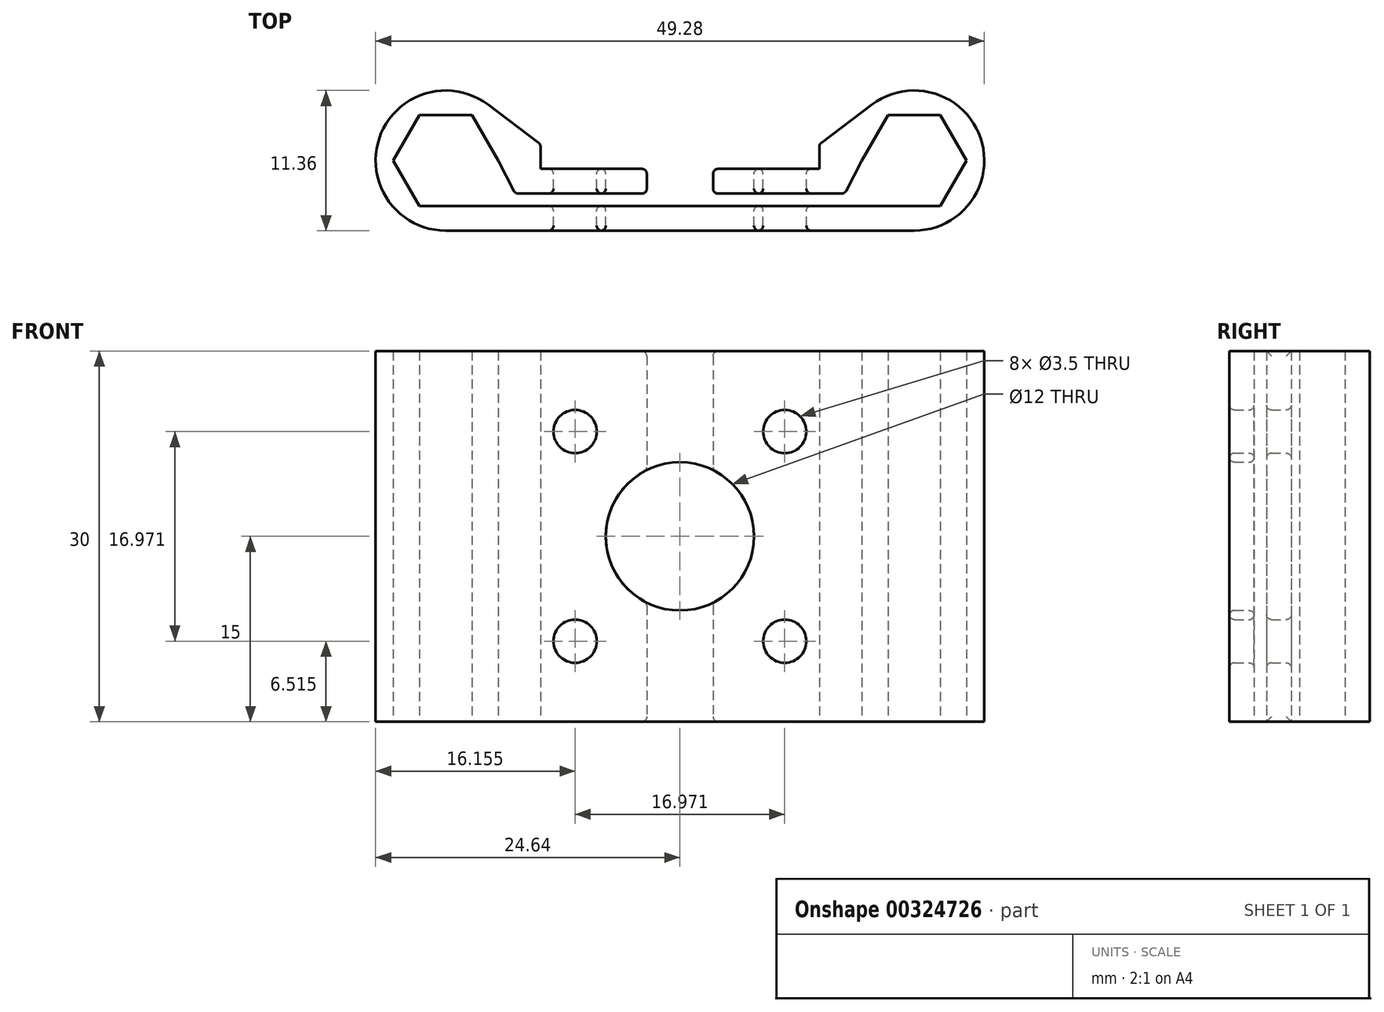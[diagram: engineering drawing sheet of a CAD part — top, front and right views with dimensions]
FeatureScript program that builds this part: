
annotation { "Feature Type Name" : "Feature", "Feature Type Description" : "" }
export const myFeature = defineFeature(function(context is Context, id is Id, definition is map)
    precondition{}
    {
        {
            var Q0;
            Q0=qCreatedBy(makeId("Front.planeOp"),FACE);
            var sketch = newSketch(context, id + "F0", { "sketchPlane" : qUnion([Q0])});
            skCircle(sketch, "E0", {"center": v(0, 0) * mm, "radius": 17.5 * mm});
            skCircle(sketch, "E1", {"center": v(0, 0) * mm, "radius": 6 * mm});
            skLineSegment(sketch, "E2", {"start": v(12.37, 12.37) * mm, "end": v(-12.37, -12.37) * mm, "construction": true});
            skLineSegment(sketch, "E3", {"start": v(0, 0) * mm, "end": v(-17.5, 0) * mm, "construction": true});
            skLineSegment(sketch, "E4", {"start": v(12.37, -12.37) * mm, "end": v(-12.37, 12.37) * mm, "construction": true});
            skCircle(sketch, "E5.0", {"center": v(0, 0) * mm, "radius": 12 * mm, "construction": true});
            skPoint(sketch, "E6", {"position": v(-8.49, -8.49) * mm});
            skPoint(sketch, "E7", {"position": v(8.49, -8.49) * mm});
            skPoint(sketch, "E8", {"position": v(8.49, 8.49) * mm});
            skPoint(sketch, "E9", {"position": v(-8.49, 8.49) * mm});
            skCircle(sketch, "E10", {"center": v(-8.49, -8.49) * mm, "radius": 1.75 * mm});
            skCircle(sketch, "E11", {"center": v(8.49, -8.49) * mm, "radius": 1.75 * mm});
            skCircle(sketch, "E12", {"center": v(8.49, 8.49) * mm, "radius": 1.75 * mm});
            skCircle(sketch, "E13", {"center": v(-8.49, 8.49) * mm, "radius": 1.75 * mm});
            skSolve(sketch);
        }
        {
            var Q0;
            Q0=qCreatedBy(makeId("Top.planeOp"),FACE);
            var sketch = newSketch(context, id + "F1", { "sketchPlane" : qUnion([Q0])});
            skPoint(sketch, "E14.0", {"position": v(-8.49, 0) * mm});
            skPoint(sketch, "E15.0", {"position": v(8.49, 0) * mm});
            skLineSegment(sketch, "E16", {"start": v(0, 0) * mm, "end": v(-18.96, 0) * mm, "construction": true});
            skCircle(sketch, "E17.cCircle", {"center": v(-18.96, 0) * mm, "radius": 3.67 * mm, "construction": true});
            skLineSegment(sketch, "E17.0", {"start": v(-16.84, -3.68) * mm, "end": v(-21.08, -3.68) * mm});
            skLineSegment(sketch, "E17.1", {"start": v(-21.08, -3.67) * mm, "end": v(-23.2, 0) * mm});
            skLineSegment(sketch, "E17.2", {"start": v(-23.2, 0) * mm, "end": v(-21.08, 3.68) * mm});
            skLineSegment(sketch, "E17.3", {"start": v(-21.08, 3.67) * mm, "end": v(-16.84, 3.67) * mm});
            skLineSegment(sketch, "E17.4", {"start": v(-16.84, 3.67) * mm, "end": v(-14.72, 0) * mm});
            skLineSegment(sketch, "E17.5", {"start": v(-14.72, 0) * mm, "end": v(-16.84, -3.68) * mm});
            skPoint(sketch, "E17.0.midPoint", {"position": v(-18.96, -3.68) * mm});
            skLineSegment(sketch, "E18", {"start": v(0, 0) * mm, "end": v(18.96, 0) * mm, "construction": true});
            skCircle(sketch, "E19.cCircle", {"center": v(18.96, 0) * mm, "radius": 3.67 * mm, "construction": true});
            skLineSegment(sketch, "E19.0", {"start": v(21.08, -3.67) * mm, "end": v(16.84, -3.68) * mm});
            skLineSegment(sketch, "E19.1", {"start": v(16.84, -3.67) * mm, "end": v(14.72, 0) * mm});
            skLineSegment(sketch, "E19.2", {"start": v(14.72, 0) * mm, "end": v(16.84, 3.67) * mm});
            skLineSegment(sketch, "E19.3", {"start": v(16.84, 3.67) * mm, "end": v(21.08, 3.68) * mm});
            skLineSegment(sketch, "E19.4", {"start": v(21.08, 3.67) * mm, "end": v(23.2, 0) * mm});
            skLineSegment(sketch, "E19.5", {"start": v(23.2, 0) * mm, "end": v(21.08, -3.67) * mm});
            skPoint(sketch, "E19.0.midPoint", {"position": v(18.96, -3.67) * mm});
            skLineSegment(sketch, "E20", {"start": v(16.84, -3.67) * mm, "end": v(-16.84, -3.68) * mm});
            skCircle(sketch, "E21.0", {"center": v(-18.96, 0) * mm, "radius": 5.67 * mm});
            skCircle(sketch, "E22.0", {"center": v(18.96, 0) * mm, "radius": 5.67 * mm});
            skLineSegment(sketch, "E23", {"start": v(-18.96, -5.68) * mm, "end": v(18.96, -5.67) * mm});
            skPoint(sketch, "E24", {"position": v(-11.29, 0) * mm});
            skPoint(sketch, "E25", {"position": v(-5.69, 0) * mm});
            skLineSegment(sketch, "E26.0", {"start": v(15.55, -2.67) * mm, "end": v(-15.55, -2.68) * mm, "construction": true});
            skLineSegment(sketch, "E27", {"start": v(-14.62, -2.68) * mm, "end": v(-2.69, -2.67) * mm});
            skLineSegment(sketch, "E28", {"start": v(-2.69, -2.67) * mm, "end": v(-2.69, -0.67) * mm});
            skLineSegment(sketch, "E29", {"start": v(-2.69, -0.67) * mm, "end": v(-13.33, -0.67) * mm});
            skLineSegment(sketch, "E30", {"start": v(-11.29, -2.68) * mm, "end": v(-11.29, -0.68) * mm, "construction": true});
            skLineSegment(sketch, "E31", {"start": v(-5.69, -2.67) * mm, "end": v(-5.69, -0.67) * mm, "construction": true});
            skLineSegment(sketch, "E32", {"start": v(-15.55, 4.53) * mm, "end": v(-11.29, 1.32) * mm});
            skLineSegment(sketch, "E33", {"start": v(-11.29, 1.32) * mm, "end": v(-11.29, -0.68) * mm});
            skLineSegment(sketch, "E34", {"start": v(-14.72, 0) * mm, "end": v(-13.33, -2.68) * mm});
            skLineSegment(sketch, "E35", {"start": v(0, 0) * mm, "end": v(0, -5.68) * mm, "construction": true});
            skLineSegment(sketch, "E36.MirrorCS", {"start": v(15.55, 4.53) * mm, "end": v(11.29, 1.32) * mm});
            skLineSegment(sketch, "E37.MirrorCS", {"start": v(11.29, 1.32) * mm, "end": v(11.29, -0.68) * mm});
            skLineSegment(sketch, "E38.MirrorCS", {"start": v(2.69, -0.67) * mm, "end": v(13.33, -0.67) * mm});
            skLineSegment(sketch, "E39.MirrorCS", {"start": v(2.69, -2.67) * mm, "end": v(2.69, -0.67) * mm});
            skLineSegment(sketch, "E40.MirrorCS", {"start": v(-15.55, -2.67) * mm, "end": v(15.55, -2.68) * mm, "construction": true});
            skLineSegment(sketch, "E41.MirrorCS", {"start": v(14.72, 0) * mm, "end": v(13.33, -2.68) * mm});
            skLineSegment(sketch, "E42", {"start": v(2.69, -2.67) * mm, "end": v(13.33, -2.67) * mm});
            skSolve(sketch);
        }
        {
            var Q0;
            {var subQ5=sQuery(id+"F1.wireOp",EDGE,"E23");Q0=makeQuery(id+"F1.imprint","IMPRINT",FACE,{"disambiguationData":[TD([[makeQuery(id+"F1.imprint","IMPRINT",EDGE,{"derivedFrom":subQ5}),1.0]])]});}
            var Q1;
            {var subQ9=sQuery(id+"F1.wireOp",EDGE,"E17.0");Q1=makeQuery(id+"F1.imprint","IMPRINT",FACE,{"disambiguationData":[TD([[makeQuery(id+"F1.imprint","IMPRINT",EDGE,{"derivedFrom":subQ9}),1.0]])]});}
            var Q2;
            {var subQ1=sQuery(id+"F1.wireOp",EDGE,"E28");Q2=makeQuery(id+"F1.imprint","IMPRINT",FACE,{"disambiguationData":[TD([[makeQuery(id+"F1.imprint","IMPRINT",EDGE,{"derivedFrom":subQ1}),1.0]])]});}
            var Q3;
            {var subQ3=sQuery(id+"F1.wireOp",EDGE,"E32");Q3=makeQuery(id+"F1.imprint","IMPRINT",FACE,{"disambiguationData":[TD([[makeQuery(id+"F1.imprint","IMPRINT",EDGE,{"derivedFrom":subQ3}),-1.0]])]});}
            var Q4;
            {var subQ6=sQuery(id+"F1.wireOp",EDGE,"E19.0");Q4=makeQuery(id+"F1.imprint","IMPRINT",FACE,{"disambiguationData":[TD([[makeQuery(id+"F1.imprint","IMPRINT",EDGE,{"derivedFrom":subQ6}),1.0]])]});}
            var Q5;
            {var subQ0=sQuery(id+"F1.wireOp",EDGE,"E36.MirrorCS");Q5=makeQuery(id+"F1.imprint","IMPRINT",FACE,{"disambiguationData":[TD([[makeQuery(id+"F1.imprint","IMPRINT",EDGE,{"derivedFrom":subQ0}),1.0]])]});}
            var Q6;
            {var subQ0=sQuery(id+"F1.wireOp",EDGE,"E39.MirrorCS");Q6=makeQuery(id+"F1.imprint","IMPRINT",FACE,{"disambiguationData":[TD([[makeQuery(id+"F1.imprint","IMPRINT",EDGE,{"derivedFrom":subQ0}),-1.0]])]});}
            extrude(context, id + "F2", {"entities" : qUnion([Q0, Q1, Q2, Q3, Q4, Q5, Q6]), "endBound" : BoundingType.SYMMETRIC, "depth" : 30 * mm});
        }
        {
            var Q0;
            Q0=makeQuery(id+"F0.imprint","IMPRINT",FACE,{"disambiguationData":[TD([[makeQuery(id+"F0.imprint","IMPRINT",EDGE,{"derivedFrom":sQuery(id+"F0.wireOp",EDGE,"E10")}),1.0]])]});
            var Q1;
            Q1=makeQuery(id+"F0.imprint","IMPRINT",FACE,{"disambiguationData":[TD([[makeQuery(id+"F0.imprint","IMPRINT",EDGE,{"derivedFrom":sQuery(id+"F0.wireOp",EDGE,"E13")}),1.0]])]});
            var Q2;
            Q2=makeQuery(id+"F0.imprint","IMPRINT",FACE,{"disambiguationData":[TD([[makeQuery(id+"F0.imprint","IMPRINT",EDGE,{"derivedFrom":sQuery(id+"F0.wireOp",EDGE,"E11")}),1.0]])]});
            var Q3;
            Q3=makeQuery(id+"F0.imprint","IMPRINT",FACE,{"disambiguationData":[TD([[makeQuery(id+"F0.imprint","IMPRINT",EDGE,{"derivedFrom":sQuery(id+"F0.wireOp",EDGE,"E12")}),1.0]])]});
            var Q4;
            Q4=makeQuery(id+"F0.imprint","IMPRINT",FACE,{"disambiguationData":[TD([[makeQuery(id+"F0.imprint","IMPRINT",EDGE,{"derivedFrom":sQuery(id+"F0.wireOp",EDGE,"E1")}),1.0]])]});
            extrude(context, id + "F3", {"entities" : qUnion([Q0, Q1, Q2, Q3, Q4]), "operationType" : NewBodyOperationType.REMOVE, "endBound" : BoundingType.THROUGH_ALL, "depth" : 25 * mm});
        }
        {
            var Q0;
            Q0=makeQuery(id+"F2.opExtrude","SWEPT_EDGE",EDGE,{"disambiguationData":[OSD([sQuery(id+"F1.wireOp",EDGE,"E27"),sQuery(id+"F1.wireOp",EDGE,"E34")])]});
            var Q1;
            Q1=makeQuery(id+"F2.opExtrude","SWEPT_EDGE",EDGE,{"disambiguationData":[OSD([sQuery(id+"F1.wireOp",EDGE,"E41.MirrorCS"),sQuery(id+"F1.wireOp",EDGE,"E42")])]});
            var Q2;
            Q2=makeQuery(id+"F2.opExtrude","SWEPT_EDGE",EDGE,{"disambiguationData":[OSD([sQuery(id+"F1.wireOp",EDGE,"E36.MirrorCS"),sQuery(id+"F1.wireOp",EDGE,"E37.MirrorCS")])]});
            var Q3;
            Q3=makeQuery(id+"F2.opExtrude","SWEPT_EDGE",EDGE,{"disambiguationData":[OSD([sQuery(id+"F1.wireOp",EDGE,"E32"),sQuery(id+"F1.wireOp",EDGE,"E33")])]});
            var Q4;
            Q4=makeQuery(id+"F3.boolean.opBoolean","COPY",FACE,{"disambiguationData":[TD([makeQuery(id+"F2.opExtrude","SWEPT_FACE",FACE,{"disambiguationData":[OSD([sQuery(id+"F1.wireOp",EDGE,"E27")])]})])],"derivedFrom":makeQuery(id+"F3.opExtrude","SWEPT_FACE",FACE,{"disambiguationData":[OSD([sQuery(id+"F0.wireOp",EDGE,"E1")])]})});
            var Q5;
            {var subQ0=sQuery(id+"F1.wireOp",EDGE,"E29");var subQ1=sQuery(id+"F1.wireOp",EDGE,"E28");var subQ2=sQuery(id+"F1.wireOp",EDGE,"E27");Q5=makeQuery(id+"F3.boolean.opBoolean","SPLIT",FACE,{"disambiguationData":[TD([makeQuery(id+"F2.opExtrude","CAP_FACE",FACE,{"disambiguationData":[OSD([sQuery(id+"F1.wireOp",EDGE,"E17.0"),sQuery(id+"F1.wireOp",EDGE,"E17.1"),sQuery(id+"F1.wireOp",EDGE,"E17.2"),sQuery(id+"F1.wireOp",EDGE,"E17.3"),sQuery(id+"F1.wireOp",EDGE,"E17.4"),sQuery(id+"F1.wireOp",EDGE,"E19.0"),sQuery(id+"F1.wireOp",EDGE,"E19.2"),sQuery(id+"F1.wireOp",EDGE,"E19.3"),sQuery(id+"F1.wireOp",EDGE,"E19.4"),sQuery(id+"F1.wireOp",EDGE,"E19.5"),sQuery(id+"F1.wireOp",EDGE,"E20"),sQuery(id+"F1.wireOp",EDGE,"E21.0"),sQuery(id+"F1.wireOp",EDGE,"E22.0"),sQuery(id+"F1.wireOp",EDGE,"E23"),subQ2,subQ1,subQ0,sQuery(id+"F1.wireOp",EDGE,"E32"),sQuery(id+"F1.wireOp",EDGE,"E33"),sQuery(id+"F1.wireOp",EDGE,"E34"),sQuery(id+"F1.wireOp",EDGE,"E36.MirrorCS"),sQuery(id+"F1.wireOp",EDGE,"E37.MirrorCS"),sQuery(id+"F1.wireOp",EDGE,"E38.MirrorCS"),sQuery(id+"F1.wireOp",EDGE,"E39.MirrorCS"),sQuery(id+"F1.wireOp",EDGE,"E41.MirrorCS"),sQuery(id+"F1.wireOp",EDGE,"E42")])],"isStart":false})])],"derivedFrom":makeQuery(id+"F2.opExtrude","SWEPT_FACE",FACE,{"disambiguationData":[OSD([subQ1])]})});}
            var Q6;
            {var subQ0=sQuery(id+"F1.wireOp",EDGE,"E29");var subQ1=sQuery(id+"F1.wireOp",EDGE,"E28");var subQ2=sQuery(id+"F1.wireOp",EDGE,"E27");Q6=makeQuery(id+"F3.boolean.opBoolean","SPLIT",FACE,{"disambiguationData":[TD([makeQuery(id+"F2.opExtrude","CAP_FACE",FACE,{"disambiguationData":[OSD([sQuery(id+"F1.wireOp",EDGE,"E17.0"),sQuery(id+"F1.wireOp",EDGE,"E17.1"),sQuery(id+"F1.wireOp",EDGE,"E17.2"),sQuery(id+"F1.wireOp",EDGE,"E17.3"),sQuery(id+"F1.wireOp",EDGE,"E17.4"),sQuery(id+"F1.wireOp",EDGE,"E19.0"),sQuery(id+"F1.wireOp",EDGE,"E19.2"),sQuery(id+"F1.wireOp",EDGE,"E19.3"),sQuery(id+"F1.wireOp",EDGE,"E19.4"),sQuery(id+"F1.wireOp",EDGE,"E19.5"),sQuery(id+"F1.wireOp",EDGE,"E20"),sQuery(id+"F1.wireOp",EDGE,"E21.0"),sQuery(id+"F1.wireOp",EDGE,"E22.0"),sQuery(id+"F1.wireOp",EDGE,"E23"),subQ2,subQ1,subQ0,sQuery(id+"F1.wireOp",EDGE,"E32"),sQuery(id+"F1.wireOp",EDGE,"E33"),sQuery(id+"F1.wireOp",EDGE,"E34"),sQuery(id+"F1.wireOp",EDGE,"E36.MirrorCS"),sQuery(id+"F1.wireOp",EDGE,"E37.MirrorCS"),sQuery(id+"F1.wireOp",EDGE,"E38.MirrorCS"),sQuery(id+"F1.wireOp",EDGE,"E39.MirrorCS"),sQuery(id+"F1.wireOp",EDGE,"E41.MirrorCS"),sQuery(id+"F1.wireOp",EDGE,"E42")])],"isStart":true})])],"derivedFrom":makeQuery(id+"F2.opExtrude","SWEPT_FACE",FACE,{"disambiguationData":[OSD([subQ1])]})});}
            var Q7;
            {var subQ0=sQuery(id+"F1.wireOp",EDGE,"E42");var subQ1=sQuery(id+"F1.wireOp",EDGE,"E39.MirrorCS");var subQ2=sQuery(id+"F1.wireOp",EDGE,"E38.MirrorCS");Q7=makeQuery(id+"F3.boolean.opBoolean","SPLIT",FACE,{"disambiguationData":[TD([makeQuery(id+"F2.opExtrude","CAP_FACE",FACE,{"disambiguationData":[OSD([sQuery(id+"F1.wireOp",EDGE,"E17.0"),sQuery(id+"F1.wireOp",EDGE,"E17.1"),sQuery(id+"F1.wireOp",EDGE,"E17.2"),sQuery(id+"F1.wireOp",EDGE,"E17.3"),sQuery(id+"F1.wireOp",EDGE,"E17.4"),sQuery(id+"F1.wireOp",EDGE,"E19.0"),sQuery(id+"F1.wireOp",EDGE,"E19.2"),sQuery(id+"F1.wireOp",EDGE,"E19.3"),sQuery(id+"F1.wireOp",EDGE,"E19.4"),sQuery(id+"F1.wireOp",EDGE,"E19.5"),sQuery(id+"F1.wireOp",EDGE,"E20"),sQuery(id+"F1.wireOp",EDGE,"E21.0"),sQuery(id+"F1.wireOp",EDGE,"E22.0"),sQuery(id+"F1.wireOp",EDGE,"E23"),sQuery(id+"F1.wireOp",EDGE,"E27"),sQuery(id+"F1.wireOp",EDGE,"E28"),sQuery(id+"F1.wireOp",EDGE,"E29"),sQuery(id+"F1.wireOp",EDGE,"E32"),sQuery(id+"F1.wireOp",EDGE,"E33"),sQuery(id+"F1.wireOp",EDGE,"E34"),sQuery(id+"F1.wireOp",EDGE,"E36.MirrorCS"),sQuery(id+"F1.wireOp",EDGE,"E37.MirrorCS"),subQ2,subQ1,sQuery(id+"F1.wireOp",EDGE,"E41.MirrorCS"),subQ0])],"isStart":false})])],"derivedFrom":makeQuery(id+"F2.opExtrude","SWEPT_FACE",FACE,{"disambiguationData":[OSD([subQ1])]})});}
            var Q8;
            Q8=makeQuery(id+"F3.boolean.opBoolean","COPY",FACE,{"disambiguationData":[TD([makeQuery(id+"F2.opExtrude","SWEPT_FACE",FACE,{"disambiguationData":[OSD([sQuery(id+"F1.wireOp",EDGE,"E38.MirrorCS")])]})])],"derivedFrom":makeQuery(id+"F3.opExtrude","SWEPT_FACE",FACE,{"disambiguationData":[OSD([sQuery(id+"F0.wireOp",EDGE,"E1")])]})});
            var Q9;
            {var subQ0=sQuery(id+"F1.wireOp",EDGE,"E42");var subQ1=sQuery(id+"F1.wireOp",EDGE,"E39.MirrorCS");var subQ2=sQuery(id+"F1.wireOp",EDGE,"E38.MirrorCS");Q9=makeQuery(id+"F3.boolean.opBoolean","SPLIT",FACE,{"disambiguationData":[TD([makeQuery(id+"F2.opExtrude","CAP_FACE",FACE,{"disambiguationData":[OSD([sQuery(id+"F1.wireOp",EDGE,"E17.0"),sQuery(id+"F1.wireOp",EDGE,"E17.1"),sQuery(id+"F1.wireOp",EDGE,"E17.2"),sQuery(id+"F1.wireOp",EDGE,"E17.3"),sQuery(id+"F1.wireOp",EDGE,"E17.4"),sQuery(id+"F1.wireOp",EDGE,"E19.0"),sQuery(id+"F1.wireOp",EDGE,"E19.2"),sQuery(id+"F1.wireOp",EDGE,"E19.3"),sQuery(id+"F1.wireOp",EDGE,"E19.4"),sQuery(id+"F1.wireOp",EDGE,"E19.5"),sQuery(id+"F1.wireOp",EDGE,"E20"),sQuery(id+"F1.wireOp",EDGE,"E21.0"),sQuery(id+"F1.wireOp",EDGE,"E22.0"),sQuery(id+"F1.wireOp",EDGE,"E23"),sQuery(id+"F1.wireOp",EDGE,"E27"),sQuery(id+"F1.wireOp",EDGE,"E28"),sQuery(id+"F1.wireOp",EDGE,"E29"),sQuery(id+"F1.wireOp",EDGE,"E32"),sQuery(id+"F1.wireOp",EDGE,"E33"),sQuery(id+"F1.wireOp",EDGE,"E34"),sQuery(id+"F1.wireOp",EDGE,"E36.MirrorCS"),sQuery(id+"F1.wireOp",EDGE,"E37.MirrorCS"),subQ2,subQ1,sQuery(id+"F1.wireOp",EDGE,"E41.MirrorCS"),subQ0])],"isStart":true})])],"derivedFrom":makeQuery(id+"F2.opExtrude","SWEPT_FACE",FACE,{"disambiguationData":[OSD([subQ1])]})});}
            var Q10;
            Q10=makeQuery(id+"F3.boolean.opBoolean","COPY",FACE,{"disambiguationData":[TD([makeQuery(id+"F2.opExtrude","SWEPT_FACE",FACE,{"disambiguationData":[OSD([sQuery(id+"F1.wireOp",EDGE,"E23")])]})])],"derivedFrom":makeQuery(id+"F3.opExtrude","SWEPT_FACE",FACE,{"disambiguationData":[OSD([sQuery(id+"F0.wireOp",EDGE,"E1")])]})});
            var Q11;
            Q11=makeQuery(id+"F3.boolean.opBoolean","COPY",FACE,{"disambiguationData":[TD([makeQuery(id+"F2.opExtrude","SWEPT_FACE",FACE,{"disambiguationData":[OSD([sQuery(id+"F1.wireOp",EDGE,"E23")])]})])],"derivedFrom":makeQuery(id+"F3.opExtrude","SWEPT_FACE",FACE,{"disambiguationData":[OSD([sQuery(id+"F0.wireOp",EDGE,"E13")])]})});
            var Q12;
            Q12=makeQuery(id+"F3.boolean.opBoolean","COPY",FACE,{"disambiguationData":[TD([makeQuery(id+"F2.opExtrude","SWEPT_FACE",FACE,{"disambiguationData":[OSD([sQuery(id+"F1.wireOp",EDGE,"E27")])]})])],"derivedFrom":makeQuery(id+"F3.opExtrude","SWEPT_FACE",FACE,{"disambiguationData":[OSD([sQuery(id+"F0.wireOp",EDGE,"E13")])]})});
            var Q13;
            Q13=makeQuery(id+"F3.boolean.opBoolean","COPY",FACE,{"disambiguationData":[TD([makeQuery(id+"F2.opExtrude","SWEPT_FACE",FACE,{"disambiguationData":[OSD([sQuery(id+"F1.wireOp",EDGE,"E23")])]})])],"derivedFrom":makeQuery(id+"F3.opExtrude","SWEPT_FACE",FACE,{"disambiguationData":[OSD([sQuery(id+"F0.wireOp",EDGE,"E10")])]})});
            var Q14;
            Q14=makeQuery(id+"F3.boolean.opBoolean","COPY",FACE,{"disambiguationData":[TD([makeQuery(id+"F2.opExtrude","SWEPT_FACE",FACE,{"disambiguationData":[OSD([sQuery(id+"F1.wireOp",EDGE,"E27")])]})])],"derivedFrom":makeQuery(id+"F3.opExtrude","SWEPT_FACE",FACE,{"disambiguationData":[OSD([sQuery(id+"F0.wireOp",EDGE,"E10")])]})});
            var Q15;
            Q15=makeQuery(id+"F3.boolean.opBoolean","COPY",FACE,{"disambiguationData":[TD([makeQuery(id+"F2.opExtrude","SWEPT_FACE",FACE,{"disambiguationData":[OSD([sQuery(id+"F1.wireOp",EDGE,"E23")])]})])],"derivedFrom":makeQuery(id+"F3.opExtrude","SWEPT_FACE",FACE,{"disambiguationData":[OSD([sQuery(id+"F0.wireOp",EDGE,"E11")])]})});
            var Q16;
            Q16=makeQuery(id+"F3.boolean.opBoolean","COPY",FACE,{"disambiguationData":[TD([makeQuery(id+"F2.opExtrude","SWEPT_FACE",FACE,{"disambiguationData":[OSD([sQuery(id+"F1.wireOp",EDGE,"E38.MirrorCS")])]})])],"derivedFrom":makeQuery(id+"F3.opExtrude","SWEPT_FACE",FACE,{"disambiguationData":[OSD([sQuery(id+"F0.wireOp",EDGE,"E11")])]})});
            var Q17;
            Q17=makeQuery(id+"F3.boolean.opBoolean","COPY",FACE,{"disambiguationData":[TD([makeQuery(id+"F2.opExtrude","SWEPT_FACE",FACE,{"disambiguationData":[OSD([sQuery(id+"F1.wireOp",EDGE,"E23")])]})])],"derivedFrom":makeQuery(id+"F3.opExtrude","SWEPT_FACE",FACE,{"disambiguationData":[OSD([sQuery(id+"F0.wireOp",EDGE,"E12")])]})});
            var Q18;
            Q18=makeQuery(id+"F3.boolean.opBoolean","COPY",FACE,{"disambiguationData":[TD([makeQuery(id+"F2.opExtrude","SWEPT_FACE",FACE,{"disambiguationData":[OSD([sQuery(id+"F1.wireOp",EDGE,"E38.MirrorCS")])]})])],"derivedFrom":makeQuery(id+"F3.opExtrude","SWEPT_FACE",FACE,{"disambiguationData":[OSD([sQuery(id+"F0.wireOp",EDGE,"E12")])]})});
            fillet(context, id + "F4", {"entities" : qUnion([Q0, Q1, Q2, Q3, Q4, Q5, Q6, Q7, Q8, Q9, Q10, Q11, Q12, Q13, Q14, Q15, Q16, Q17, Q18]), "radius" : 0.4 * mm, "allowEdgeOverflow" : false});
        }
    });
